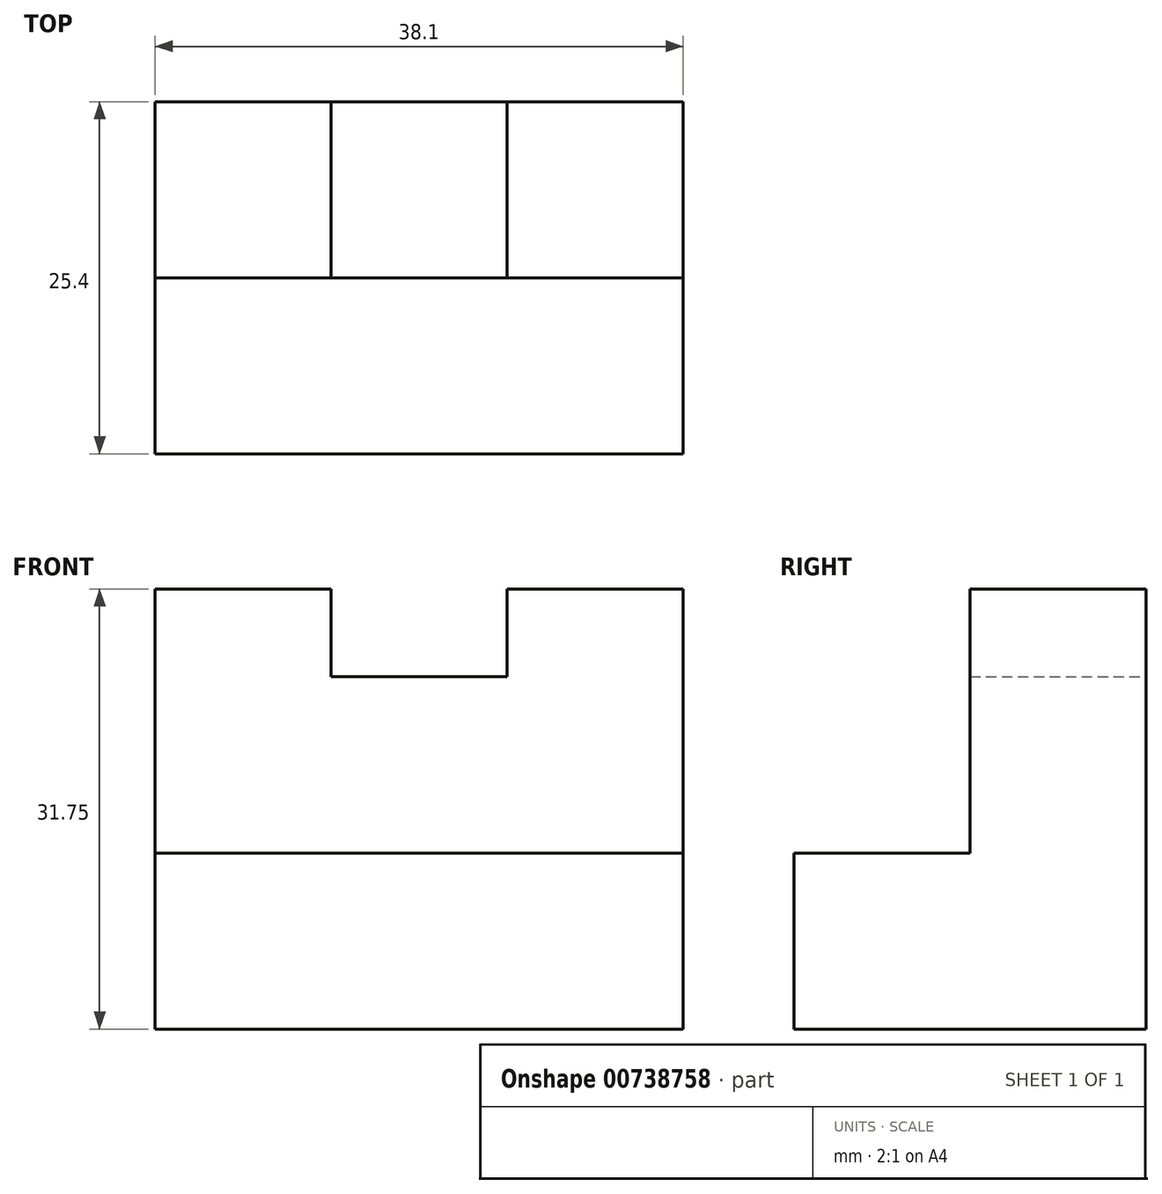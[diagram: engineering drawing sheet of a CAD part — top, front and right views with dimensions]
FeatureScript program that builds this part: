
annotation { "Feature Type Name" : "Feature", "Feature Type Description" : "" }
export const myFeature = defineFeature(function(context is Context, id is Id, definition is map)
    precondition{}
    {
        {
            var Q0;
            Q0=qCreatedBy(makeId("Right.planeOp"),FACE);
            var sketch = newSketch(context, id + "F0", { "sketchPlane" : qUnion([Q0])});
            skLineSegment(sketch, "E0", {"start": v(0, 0) * mm, "end": v(0, 31.75) * mm});
            skLineSegment(sketch, "E1", {"start": v(0, 31.75) * mm, "end": v(-12.7, 31.75) * mm});
            skLineSegment(sketch, "E2", {"start": v(-12.7, 31.75) * mm, "end": v(-12.7, 12.7) * mm});
            skLineSegment(sketch, "E3", {"start": v(-12.7, 12.7) * mm, "end": v(-25.4, 12.7) * mm});
            skLineSegment(sketch, "E4", {"start": v(-25.4, 12.7) * mm, "end": v(-25.4, 0) * mm});
            skLineSegment(sketch, "E5", {"start": v(-25.4, 0) * mm, "end": v(0, 0) * mm});
            skSolve(sketch);
        }
        {
            var Q0;
            Q0 = qSketchRegion(id + "F0", true);
            extrude(context, id + "F1", {"entities" : qUnion([Q0]), "depth" : 38.1 * mm, "offsetDistance" : 25.4 * mm});
        }
        {
            var Q0;
            Q0=qCreatedBy(makeId("Front.planeOp"),FACE);
            var sketch = newSketch(context, id + "F2", { "sketchPlane" : qUnion([Q0])});
            skLineSegment(sketch, "E6", {"start": v(12.7, 31.76) * mm, "end": v(12.7, 25.41) * mm});
            skLineSegment(sketch, "E7", {"start": v(12.7, 25.41) * mm, "end": v(25.4, 25.41) * mm});
            skLineSegment(sketch, "E8", {"start": v(25.4, 25.41) * mm, "end": v(25.4, 31.76) * mm});
            skLineSegment(sketch, "E9", {"start": v(25.4, 31.76) * mm, "end": v(12.7, 31.76) * mm});
            skSolve(sketch);
        }
        {
            var Q0;
            Q0 = qSketchRegion(id + "F2", true);
            extrude(context, id + "F3", {"entities" : qUnion([Q0]), "operationType" : NewBodyOperationType.REMOVE, "depth" : 12.7 * mm, "offsetDistance" : 25.4 * mm});
        }
    });
